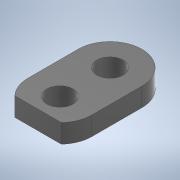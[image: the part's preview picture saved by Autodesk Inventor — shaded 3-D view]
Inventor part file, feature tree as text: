
AUTODESK INVENTOR PART (.ipt)
format: ipt  version: 2020 (Build 240168000, 168)  size: 249,856 bytes
history: native  units: mm
features: extrude x2, sketch x2
ambient origin geometry x8: Origin, YZ Plane, XZ Plane, XY Plane, X Axis, Y Axis, Z Axis, Center Point
bodies: Volumenkörper1 (feature_tree)
feature tree (4):
  extrude  "Extrusion1"  Depth=3.0mm
  extrude  "Extrusion2"  Depth=3.0mm TaperAngle=0.0deg
  sketch  "Skizze1"  dims[d0=4.2mm d1=3.0mm]
  sketch  "Skizze2"  dims[d2=8.0mm d3=3.0mm d4=0.0mm d5=3.5mm d6=10.0mm d7=0.0mm]
